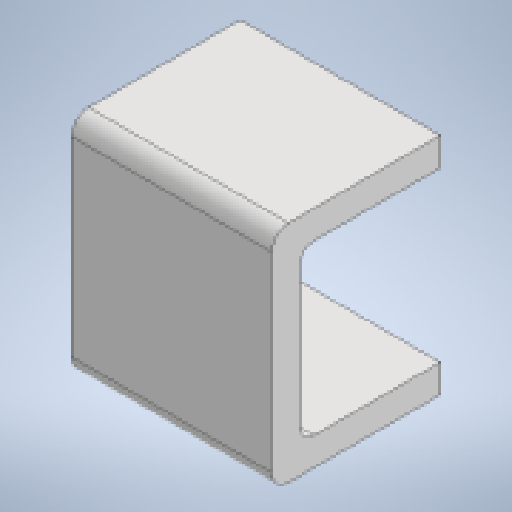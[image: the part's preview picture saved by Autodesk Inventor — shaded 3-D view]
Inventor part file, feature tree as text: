
AUTODESK INVENTOR PART (.ipt)
format: ipt  version: 2023 (Build 270158000, 158)  size: 521,728 bytes
history: native  units: in
note: dims shown in document units (in); Inventor stores cm internally (conversion verified against a paired STEP export)
features: extrude x14, sketch x14, other x12, reference x8, projected_geometry x6, fillet x3, mirror x1
ambient origin geometry x8: Origin, YZ Plane, XZ Plane, XY Plane, X Axis, Y Axis, Z Axis, Center Point
bodies: Solid2 (feature_tree)
feature tree (58):
  other  "Bryła1"
  extrude  "Wyciągnięcie proste1"  TaperAngle=0.0deg  [1 undecoded]
  extrude  "Wyciągnięcie proste2"  Depth=0.2559in
  extrude  "Wyciągnięcie proste3"  Depth=0.1181in
  extrude  "Wyciągnięcie proste4"  Depth=0.2165in
  extrude  "Wyciągnięcie proste5"  Depth=0.3937in
  extrude  "Wyciągnięcie proste6"  Depth=0.1772in TaperAngle=0.0deg
  extrude  "Wyciągnięcie proste7"  Depth=0.0591in
  extrude  "Wyciągnięcie proste8"  Depth=0.1772in TaperAngle=0.0deg
  extrude  "Wyciągnięcie proste9"  Depth=0.3937in TaperAngle=0.0deg
  fillet  "Zaokrąglenie1"  Radius=0.0787in
  other  "Edytuj bezpośrednio1"
  other  "Edytuj bezpośrednio2"
  extrude  "Wyciągnięcie proste10"  Depth=0.1181in
  other  "Edytuj bezpośrednio3"
  extrude  "Wyciągnięcie proste11"  Depth=0.0748in TaperAngle=0.0deg
  other  "Płaszczyzna konstrukcyjna1"
  mirror  "Odbij1"
  extrude  "Wyciągnięcie proste12"  Depth=0.1181in
  fillet  "Zaokrąglenie2"  Radius=0.1181in
  extrude  "Wyciągnięcie proste13"  Depth=0.0787in
  fillet  "Zaokrąglenie3"  Radius=0.2165in
  extrude  "Wyciągnięcie proste14"  Depth=0.0787in
  sketch  "Szkic1"
  projected_geometry  "Pętla rzutowana1"
  reference  "Odniesienie1"
  sketch  "Szkic2"
  reference  "Odniesienie2"
  sketch  "Szkic3"
  projected_geometry  "Pętla rzutowana2"
  sketch  "Szkic4"
  reference  "Odniesienie3"
  sketch  "Szkic5"
  projected_geometry  "Pętla rzutowana3"
  sketch  "Szkic6"
  reference  "Odniesienie4"
  sketch  "Szkic7"
  reference  "Odniesienie5"
  reference  "Odniesienie6"
  reference  "Odniesienie7"
  sketch  "Szkic8"
  sketch  "Szkic9"
  projected_geometry  "Pętla rzutowana4"
  sketch  "Szkic10"
  projected_geometry  "Pętla rzutowana5"
  sketch  "Szkic11"
  sketch  "Szkic12"
  sketch  "Szkic13"
  reference  "Odniesienie8"
  sketch  "Szkic14"
  projected_geometry  "Pętla rzutowana6"
  other  "Zespół3"
  other  "minisumopodsr:1"
  other  "n20 motor:2"
  other  "n20 motor:1"
  other  "Przesuń1"
  other  "Przesuń2"
  other  "Przesuń3"
note: 1 required parameter value undecoded (feature->parameter linkage not recoverable at this tier; creation-order binding heuristic only, values carry confidence <= 0.55)
